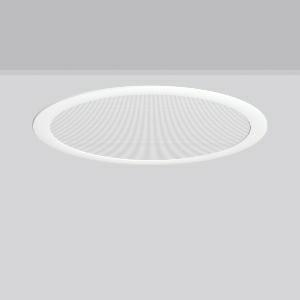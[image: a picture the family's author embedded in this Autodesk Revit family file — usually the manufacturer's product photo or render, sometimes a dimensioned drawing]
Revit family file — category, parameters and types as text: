
# Revit family: toledo_flat_round_e_901669_002_76_47d0
name_source: partatom
category: Lighting Fixtures
units: mm (PartAtom-declared; Revit-internal decimal feet)

## family parameters
Cut with Voids When Loaded = No
Host = Face
Light Source = No
Part Type = Normal
Room Calculation Point = No
Round Connector Dimension = Use Diameter
Shared = No

## types (1)
- TuneableWhite 846 (1 x LED Modul 846, 2900 lm, 4600)
    Apparent Load = 30 VA
    CIE Flux Codes = 63 87 96 100 100
    Color Rendering = 80
    Color Temperature = 4600
    Default Elevation = 1800 mm
    Description = Series: TOLEDO FLAT round
Ultra thin recessed downlight. Housing: die-cast aluminium. Lightguide and diffuser made of non-yellowing PMMA, prismatic. Diffuser: transparent plastic, microprismatic. Tunable white dynamically adjustable from 2700 K to 6500 K. Ceiling installation with spring system. Mounting depth depends on ceiling strength. Including separate LED converter with connecting cable 250 mm. Suitable for through-wiring with separately available accessories. Surface mounted housing as accessory for all sizes. Retrofittable decorative cylinders made of chintz fabric as accessory, optional with satin finish plastic diffuser. Through-wiring box (5 pole) available as accessory. 
Colour: white
Diameter: 495 mm
Height: 6 mm
Cut-out diameter: 470 mm
Recess height: 35-55 mm
Luminaire: recess height: 31-51 mm
Lamp: LED
Socket: without socket
Colour temperature: 2700K - 6500K
Colour rendering index (CRI): 80
System power: 30 W
Rated luminous flux: 2900 lm
Luminous efficiency: 97 lm/W
System power 2: 30 W
Rated luminous flux 2: 2550 lm
Luminous efficiency 2: 85 lm/W
System power 3: 30 W
Rated luminous flux 3: 2850 lm
Luminous efficiency 3: 95 lm/W
Control gear: Converter, dimmable, DALI
Protection class: II
Type of protection: IP 54
    Height = 0 mm  [stored 0 ft]
    Lamp = 1 x LED Modul 846
    Lamp Light Flux = 2900 lm
    Lamp count = 1
    Length = 495 mm
    Lifetime = 50000 h
    Luminous efficacy = 97 lm/W
    Manufacturer = RZB
    ModVariant = No
    Model = 901669.002.76
    Mounting Place = Ceiling
    Mounting Type = Recessed
    Number of Poles = 1
    OnlyDefault = Yes
    Power Factor = 1
    Product Name = TOLEDO FLAT round E
    Product group = Recessed downlights
    ProductGroupID = 402
    Protection Class = Protection class II
    Protection Degree = IP 20
    RLX_Detail_Level = 1
    RLX_Emergency_Light_Flux = 0 lm
    RLX_Emergency_Type = 0
    RLX_Emergency_Type_DB = No
    RlxData = <blob elided: 86165 chars, md5=da3c1049>
    Socket = socket
    Standby Power = 0 W
    System Light Flux = 2900 lm
    System Power = 30 W
    Type Comments = TuneableWhite 846
    Type Image = 901586.002.jpg
    URL = http://relux.com
    VarID = tuneablewhite_846
    Voltage = 230 V
    Voltage Range = 220-240 V
    Weight = 0.00 kg
    Width = 0 mm  [stored 0 ft]

note: [stored X ft] marks values corroborated as IEEE doubles in the binary element streams (Revit-internal decimal feet)

## geometry (parser evidence)
native form markers: Blend x4, Sweep x10
no freeform markers — native parametric forms only
